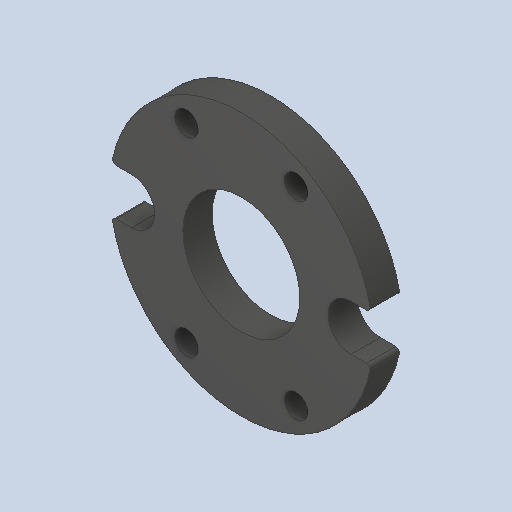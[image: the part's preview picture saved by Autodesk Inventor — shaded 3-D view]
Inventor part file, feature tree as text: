
AUTODESK INVENTOR PART (.ipt)
format: ipt  version: 2023.4 (Build 274418000, 418)  size: 119,808 bytes
history: native  units: in
note: dims shown in document units (in); Inventor stores cm internally (conversion verified against a paired STEP export)
features: fillet x1
ambient origin geometry x8: Origin, YZ Plane, XZ Plane, XY Plane, X Axis, Y Axis, Z Axis, Center Point
bodies: Solid1 (feature_tree)
feature tree (1):
  fillet  "Fillet1"  [1 undecoded]
note: 1 required parameter value undecoded (feature->parameter linkage not recoverable at this tier; creation-order binding heuristic only, values carry confidence <= 0.55)
